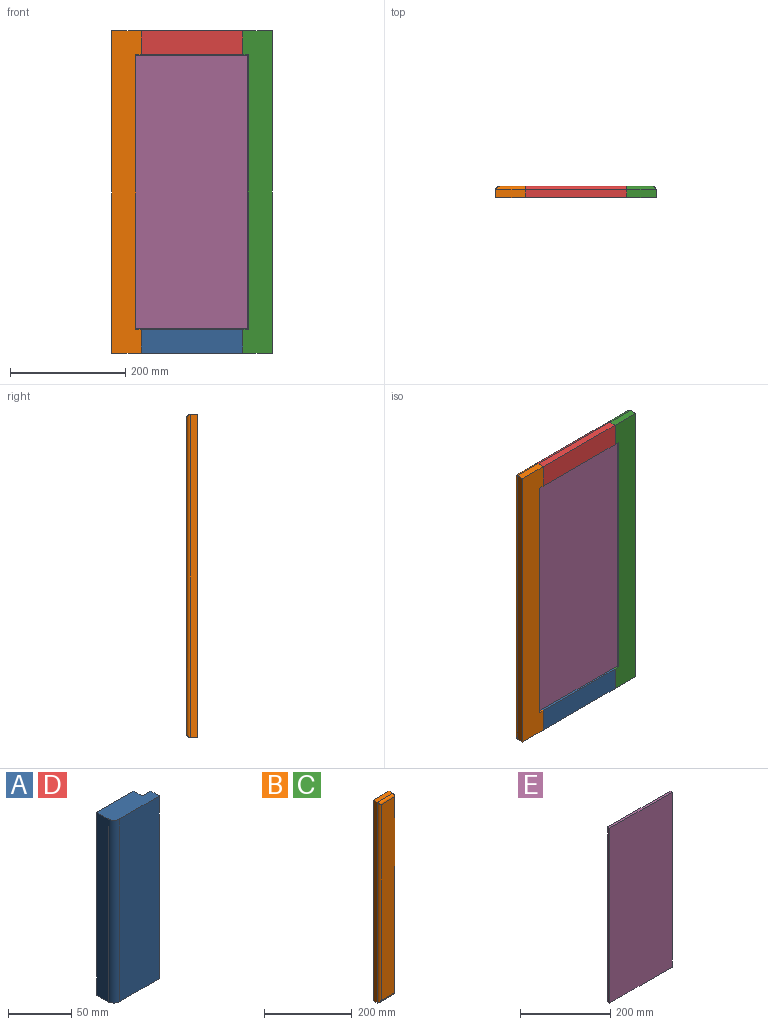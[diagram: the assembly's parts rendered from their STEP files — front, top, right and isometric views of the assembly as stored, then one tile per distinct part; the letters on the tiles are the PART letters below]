
ASSEMBLY  parts=5 mates=4
PART A: 9 faces, bbox 50.8x19.1x176.2 mm
  f0: plane 50.8x19.05mm, normal (0,0,1), area 868.4mm2, adj f2,f3,f4,f5,f6,f7,f8
  f1: plane 50.8x19.05mm, normal (0,0,-1), area 868.4mm2, adj f2,f3,f4,f5,f6,f7,f8
  f2: plane 176.21x12.7mm, normal (-1,0,0), area 2237.9mm2, adj f0,f1,f5,f6
  f3: plane 176.21x44.45mm, normal (0,-1,0), area 7832.6mm2, adj f0,f1,f4,f6
  f4: plane 176.21x9.53mm, normal (1,0,0), area 1678.4mm2, adj f0,f1,f3,f7
  f5: plane 176.21x41.28mm, normal (0,1,0), area 7273.2mm2, adj f0,f1,f2,f8
  f6: cylinder r=6.35mm len=176.21mm, axis (0,0,1), area 1757.6mm2, adj f0,f1,f2,f3
  f7: plane 176.21x9.53mm, normal (0,1,0), area 1678.4mm2, adj f0,f1,f4,f8
  f8: plane 176.21x9.53mm, normal (1,0,0), area 1678.4mm2, adj f0,f1,f5,f7
PART B: 13 faces, bbox 50.8x19.1x558.8 mm
  f0: plane 558.8x19.05mm, normal (1,0,0), area 6091.6mm2, adj f1,f3,f4,f5,f6,f7,f9,f10
  f1: plane 558.8x50.8mm, normal (0,1,0), area 23850.8mm2, adj f0,f2,f4,f5,f9,f10,f11
  f2: plane 558.8x12.7mm, normal (-1,0,0), area 7096.8mm2, adj f1,f4,f5,f8
  f3: plane 546.1x44.45mm, normal (0,-1,0), area 24274.1mm2, adj f0,f6,f7,f8
  f4: plane 50.8x12.7mm, normal (0,0,1), area 645.2mm2, adj f0,f1,f2,f6
  f5: plane 50.8x12.7mm, normal (0,0,-1), area 645.2mm2, adj f0,f1,f2,f7
  f6: cylinder r=6.35mm len=50.8mm, axis (-1,0,0), area 483.7mm2, adj f0,f3,f4,f8
  f7: cylinder r=6.35mm len=50.8mm, axis (1,0,0), area 483.7mm2, adj f0,f3,f5,f8
  f8: cylinder r=6.35mm len=558.8mm, axis (0,0,1), area 5527.8mm2, adj f2,f3,f6,f7
  f9: plane 9.53x9.53mm, normal (0,0,1), area 90.7mm2, adj f0,f1,f11,f12
  f10: plane 9.53x9.53mm, normal (0,0,-1), area 90.7mm2, adj f0,f1,f11,f12
  f11: plane 476.25x9.53mm, normal (1,0,0), area 4536.3mm2, adj f1,f9,f10,f12
  f12: plane 476.25x9.53mm, normal (0,1,0), area 4536.3mm2, adj f0,f9,f10,f11
PART C: same geometry as B
PART D: same geometry as A
PART E: 6 faces, bbox 195.3x6.4x474.7 mm
  f0: plane 474.66x6.35mm, normal (-1,0,0), area 3014.1mm2, adj f1,f3,f4,f5
  f1: plane 195.26x6.35mm, normal (0,0,-1), area 1239.9mm2, adj f0,f2,f4,f5
  f2: plane 474.66x6.35mm, normal (1,0,0), area 3014.1mm2, adj f1,f3,f4,f5
  f3: plane 195.26x6.35mm, normal (0,0,1), area 1239.9mm2, adj f0,f2,f4,f5
  f4: plane 474.66x195.26mm, normal (0,-1,0), area 92683.8mm2, adj f0,f1,f2,f3
  f5: plane 474.66x195.26mm, normal (0,1,0), area 92683.8mm2, adj f0,f1,f2,f3
PLACE A rot(axis=(-0.71,0,-0.71),180deg) t=(-198.44,0,-279.4)mm
PLACE B rot(axis=(-1,0,0),180deg) t=(-249.24,0,279.4)mm
PLACE C rot(axis=(0,0,1),180deg) t=(28.58,0,-279.4)mm
PLACE D rot(axis=(-0.71,0,0.71),180deg) t=(-22.23,0,279.4)mm
PLACE E rot(axis=(0,0,1),180deg) t=(-13.49,-15.88,-237.33)mm
MATE fastened C.f4 <-> D.f2  axis (0,0,1) through (-22.23,-12.7,279.4)mm
MATE fastened D.f0 <-> B.f0  axis (-1,0,0) through (-198.44,-19.05,279.4)mm
MATE fastened B.f0 <-> A.f1  axis (1,0,0) through (-198.44,-19.05,-279.4)mm
MATE fastened E.f4 <-> C.f12  axis (0,1,0) through (-13.49,-9.53,237.33)mm
